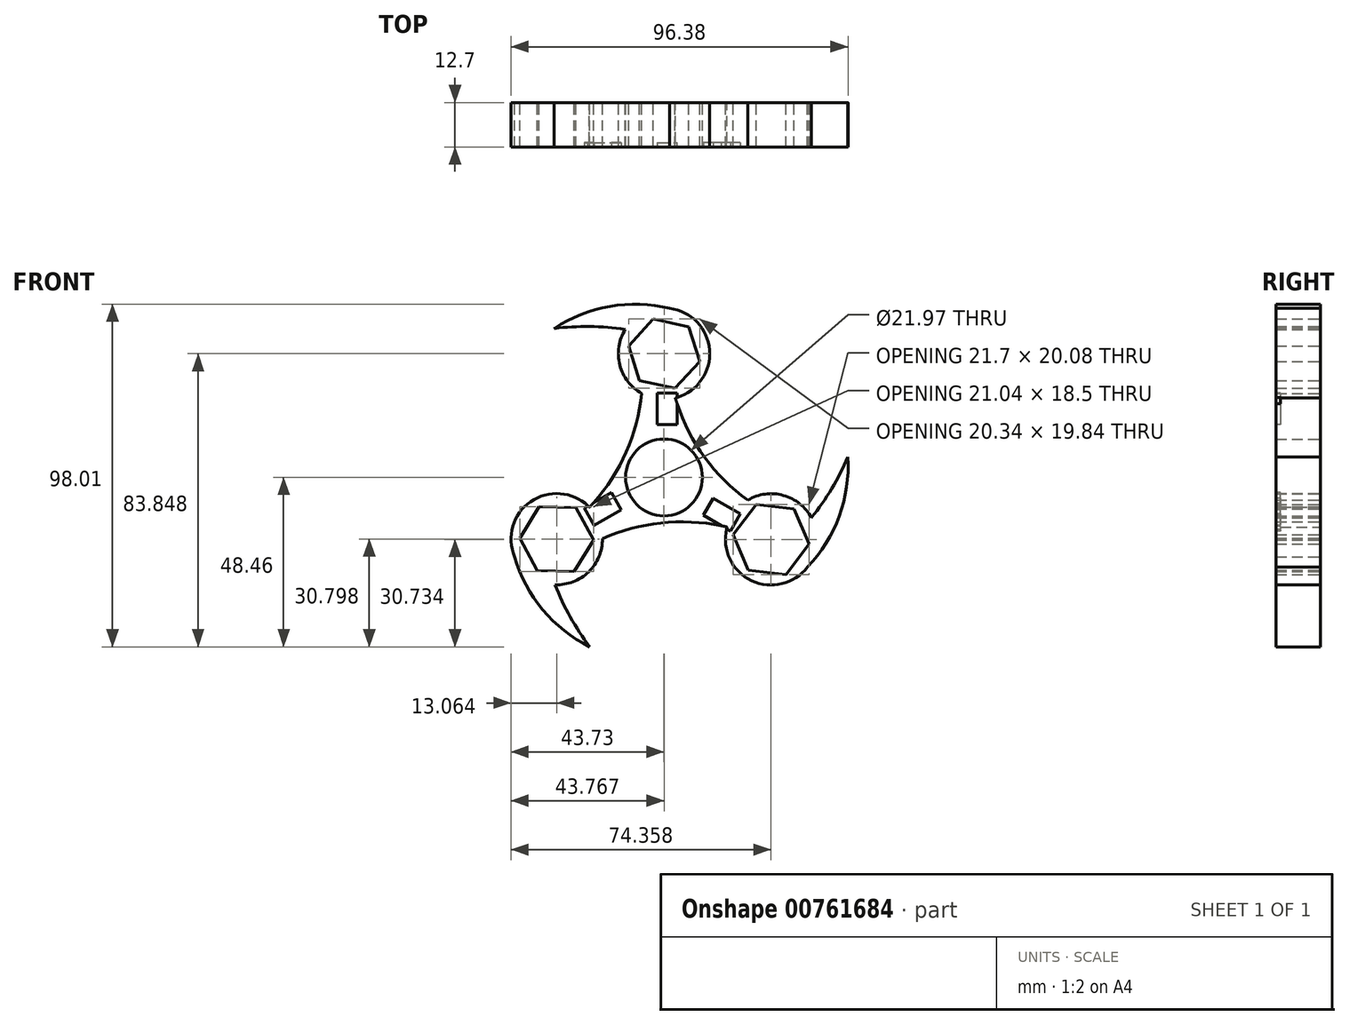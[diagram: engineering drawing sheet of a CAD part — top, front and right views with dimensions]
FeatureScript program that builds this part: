
annotation { "Feature Type Name" : "Feature", "Feature Type Description" : "" }
export const myFeature = defineFeature(function(context is Context, id is Id, definition is map)
    precondition{}
    {
        {
            var Q0;
            Q0=qCreatedBy(makeId("Front.planeOp"),FACE);
            var sketch = newSketch(context, id + "F0", { "sketchPlane" : qUnion([Q0])});
            skCircle(sketch, "E0", {"center": v(0, 0) * mm, "radius": 10.99 * mm});
            skArc(sketch, "E1", {"start": v(-21.32, -8.54) * mm, "mid": v(-11.12, 6.48) * mm, "end": v(-6.36, 24) * mm});
            skArc(sketch, "E2.1.0", {"start": v(18.06, -14.19) * mm, "mid": v(-0.04, -12.95) * mm, "end": v(-17.6, -17.5) * mm});
            skArc(sketch, "E2.2.0", {"start": v(3.26, 22.73) * mm, "mid": v(11.17, 6.39) * mm, "end": v(23.97, -6.5) * mm});
            skArc(sketch, "E3", {"start": v(-21.32, -8.54) * mm, "mid": v(-37.88, -6.78) * mm, "end": v(-42.7, -22.72) * mm});
            skArc(sketch, "E4.1.0", {"start": v(18.06, -14.19) * mm, "mid": v(24.81, -29.42) * mm, "end": v(41.03, -25.62) * mm});
            skArc(sketch, "E4.2.0", {"start": v(3.26, 22.73) * mm, "mid": v(13.07, 36.2) * mm, "end": v(1.67, 48.35) * mm});
            skLineSegment(sketch, "E5", {"start": v(3.2, 68.64) * mm, "end": v(2.33, 68.64) * mm});
            skLineSegment(sketch, "E6", {"start": v(3.17, 68.09) * mm, "end": v(3.14, 67.76) * mm});
            skLineSegment(sketch, "E7.1.2", {"start": v(-45.7, -23.97) * mm, "end": v(-45.55, -23.9) * mm});
            skLineSegment(sketch, "E7.2.1", {"start": v(44.08, -27.88) * mm, "end": v(44.08, -27.88) * mm});
            skLineSegment(sketch, "E7.2.2", {"start": v(44.08, -27.88) * mm, "end": v(44.08, -27.88) * mm});
            skLineSegment(sketch, "E7.2.9", {"start": v(49.93, -31.26) * mm, "end": v(49.85, -31.22) * mm});
            skArc(sketch, "E8.trimOffspring", {"start": v(-11.03, 42.32) * mm, "mid": v(-12.62, 32.16) * mm, "end": v(-6.36, 24) * mm});
            skLineSegment(sketch, "E9", {"start": v(-45.7, -23.97) * mm, "end": v(-45.7, -23.97) * mm});
            skPoint(sketch, "E9.endSnap0", {"position": v(-42.1, -23.97) * mm});
            skArc(sketch, "E10", {"start": v(1.67, 48.35) * mm, "mid": v(-15.44, 48.93) * mm, "end": v(-31.36, 42.6) * mm});
            skArc(sketch, "E11", {"start": v(-11.03, 42.32) * mm, "mid": v(-21.19, 43.15) * mm, "end": v(-31.36, 42.6) * mm});
            skArc(sketch, "E12.1.0", {"start": v(-42.7, -22.72) * mm, "mid": v(-34.65, -37.84) * mm, "end": v(-21.21, -48.46) * mm});
            skArc(sketch, "E12.2.0", {"start": v(41.03, -25.62) * mm, "mid": v(50.1, -11.09) * mm, "end": v(52.57, 5.86) * mm});
            skArc(sketch, "E13.1.0", {"start": v(-31.14, -30.71) * mm, "mid": v(-26.78, -39.92) * mm, "end": v(-21.21, -48.46) * mm});
            skArc(sketch, "E13.2.0", {"start": v(42.17, -11.6) * mm, "mid": v(47.96, -3.23) * mm, "end": v(52.57, 5.86) * mm});
            skArc(sketch, "E14.trimOffspring", {"start": v(42.17, -11.6) * mm, "mid": v(34.16, -5.15) * mm, "end": v(23.97, -6.5) * mm});
            skArc(sketch, "E15.trimOffspring", {"start": v(-31.14, -30.71) * mm, "mid": v(-21.54, -27) * mm, "end": v(-17.6, -17.5) * mm});
            skCircle(sketch, "E16.cCircle", {"center": v(0.04, 35.39) * mm, "radius": 9.02 * mm, "construction": true});
            skLineSegment(sketch, "E16.0", {"start": v(10.2, 33.17) * mm, "end": v(3.2, 25.47) * mm});
            skLineSegment(sketch, "E16.1", {"start": v(3.2, 25.47) * mm, "end": v(-6.97, 27.7) * mm});
            skLineSegment(sketch, "E16.2", {"start": v(-6.97, 27.7) * mm, "end": v(-10.13, 37.6) * mm});
            skLineSegment(sketch, "E16.3", {"start": v(-10.13, 37.6) * mm, "end": v(-3.12, 45.3) * mm});
            skLineSegment(sketch, "E16.4", {"start": v(-3.12, 45.3) * mm, "end": v(7.05, 43.09) * mm});
            skLineSegment(sketch, "E16.5", {"start": v(7.05, 43.09) * mm, "end": v(10.2, 33.17) * mm});
            skPoint(sketch, "E16.0.midPoint", {"position": v(6.7, 29.32) * mm});
            skPoint(sketch, "E17.0.midPoint", {"position": v(35.2, -23.95) * mm});
            skCircle(sketch, "E18.cCircle", {"center": v(-30.67, -17.66) * mm, "radius": 9.11 * mm, "construction": true});
            skLineSegment(sketch, "E18.0", {"start": v(-20.15, -17.94) * mm, "end": v(-25.65, -26.91) * mm});
            skLineSegment(sketch, "E18.1", {"start": v(-25.65, -26.91) * mm, "end": v(-36.17, -26.63) * mm});
            skLineSegment(sketch, "E18.2", {"start": v(-36.17, -26.63) * mm, "end": v(-41.19, -17.38) * mm});
            skLineSegment(sketch, "E18.3", {"start": v(-41.19, -17.38) * mm, "end": v(-35.68, -8.41) * mm});
            skLineSegment(sketch, "E18.4", {"start": v(-35.68, -8.41) * mm, "end": v(-25.16, -8.7) * mm});
            skLineSegment(sketch, "E18.5", {"start": v(-25.16, -8.7) * mm, "end": v(-20.15, -17.94) * mm});
            skPoint(sketch, "E18.0.midPoint", {"position": v(-22.9, -22.43) * mm});
            skCircle(sketch, "E19.cCircle", {"center": v(30.63, -17.73) * mm, "radius": 9.46 * mm, "construction": true});
            skLineSegment(sketch, "E19.0", {"start": v(41.48, -19.01) * mm, "end": v(34.94, -27.76) * mm});
            skLineSegment(sketch, "E19.1", {"start": v(34.94, -27.76) * mm, "end": v(24.1, -26.48) * mm});
            skLineSegment(sketch, "E19.2", {"start": v(24.1, -26.48) * mm, "end": v(19.78, -16.44) * mm});
            skLineSegment(sketch, "E19.3", {"start": v(19.78, -16.44) * mm, "end": v(26.32, -7.69) * mm});
            skLineSegment(sketch, "E19.4", {"start": v(26.32, -7.69) * mm, "end": v(37.17, -8.97) * mm});
            skLineSegment(sketch, "E19.5", {"start": v(37.17, -8.97) * mm, "end": v(41.48, -19.01) * mm});
            skPoint(sketch, "E19.0.midPoint", {"position": v(38.2, -23.39) * mm});
            skLineSegment(sketch, "E20.left", {"start": v(-41.17, -9.9) * mm, "end": v(-41.17, -27.08) * mm});
            skPoint(sketch, "E21.orphan", {"position": v(-41.17, 53.14) * mm});
            skPoint(sketch, "E20.right.start.orphan", {"position": v(60.43, 53.14) * mm});
            skSolve(sketch);
        }
        {
            var Q0;
            Q0=makeQuery(id+"F0.imprint","IMPRINT",FACE,{"disambiguationData":[TD([[makeQuery(id+"F0.imprint","IMPRINT",EDGE,{"derivedFrom":sQuery(id+"F0.wireOp",EDGE,"E0")}),-1.0]])]});
            var Q1;
            {var subQ6=sQuery(id+"F0.wireOp",EDGE,"E12.1.0");var subQ7=sQuery(id+"F0.wireOp",EDGE,"E3");var subQ8=makeQuery(id+"F0.imprint","INTERSECT",VERTEX,{"derivedFrom":[subQ7,subQ6]});Q1=makeQuery(id+"F0.imprint","IMPRINT",FACE,{"disambiguationData":[TD([[makeQuery(id+"F0.imprint","IMPRINT",EDGE,{"disambiguationData":[TD([[subQ8,1.0]])],"derivedFrom":subQ7}),1.0]])]});}
            extrude(context, id + "F1", {"entities" : qUnion([Q0, Q1]), "depth" : 12.7 * mm, "offsetDistance" : 25.4 * mm});
        }
        {
            var Q0;
            Q0=makeQuery(id+"F1.opExtrude","CAP_FACE",FACE,{"disambiguationData":[OSD([sQuery(id+"F0.wireOp",EDGE,"E0"),sQuery(id+"F0.wireOp",EDGE,"0WG9AiSf-X3DU-dKsb-HGgb-xN8fc5cjW7sx"),sQuery(id+"F0.wireOp",EDGE,"fdadf59e-989b-42ad-8ddf-04696b9882b6.1.0"),sQuery(id+"F0.wireOp",EDGE,"fdadf59e-989b-42ad-8ddf-04696b9882b6.2.0"),sQuery(id+"F0.wireOp",EDGE,"bF39NmWU-iU4a-4hSy-7ufN-n1pPgaI3Jus0"),sQuery(id+"F0.wireOp",EDGE,"e084aeda-39b3-4897-b82e-ab5990a30452.1.0"),sQuery(id+"F0.wireOp",EDGE,"e084aeda-39b3-4897-b82e-ab5990a30452.2.0")])],"isStart":false});
            var sketch = newSketch(context, id + "F2", { "sketchPlane" : qUnion([Q0])});
            skPoint(sketch, "E22.center", {"position": v(0, 0) * mm});
            skLineSegment(sketch, "E23", {"start": v(-1.89, 24.15) * mm, "end": v(3.77, 24.15) * mm});
            skLineSegment(sketch, "E24", {"start": v(3.77, 24.32) * mm, "end": v(3.77, 15.17) * mm});
            skLineSegment(sketch, "E25", {"start": v(-1.89, 24.15) * mm, "end": v(-1.89, 15.17) * mm});
            skLineSegment(sketch, "E26", {"start": v(-1.89, 15.17) * mm, "end": v(3.77, 15.17) * mm});
            skLineSegment(sketch, "E27.1.0", {"start": v(-19.97, -13.71) * mm, "end": v(-22.8, -8.81) * mm});
            skLineSegment(sketch, "E27.1.1", {"start": v(-19.97, -13.71) * mm, "end": v(-12.2, -9.22) * mm});
            skLineSegment(sketch, "E27.1.2", {"start": v(-22.94, -8.9) * mm, "end": v(-15.02, -4.32) * mm});
            skLineSegment(sketch, "E27.1.3", {"start": v(-12.2, -9.22) * mm, "end": v(-15.02, -4.32) * mm});
            skLineSegment(sketch, "E27.2.0", {"start": v(21.86, -10.44) * mm, "end": v(19.03, -15.34) * mm});
            skLineSegment(sketch, "E27.2.1", {"start": v(21.86, -10.44) * mm, "end": v(14.08, -5.95) * mm});
            skLineSegment(sketch, "E27.2.2", {"start": v(19.18, -15.42) * mm, "end": v(11.25, -10.85) * mm});
            skLineSegment(sketch, "E27.2.3", {"start": v(14.08, -5.95) * mm, "end": v(11.25, -10.85) * mm});
            skSolve(sketch);
        }
        {
            var Q0;
            Q0 = qSketchRegion(id + "F2", true);
            extrude(context, id + "F3", {"entities" : qUnion([Q0]), "operationType" : NewBodyOperationType.REMOVE, "oppositeDirection" : true, "depth" : 1.27 * mm, "offsetDistance" : 25.4 * mm});
        }
    });
